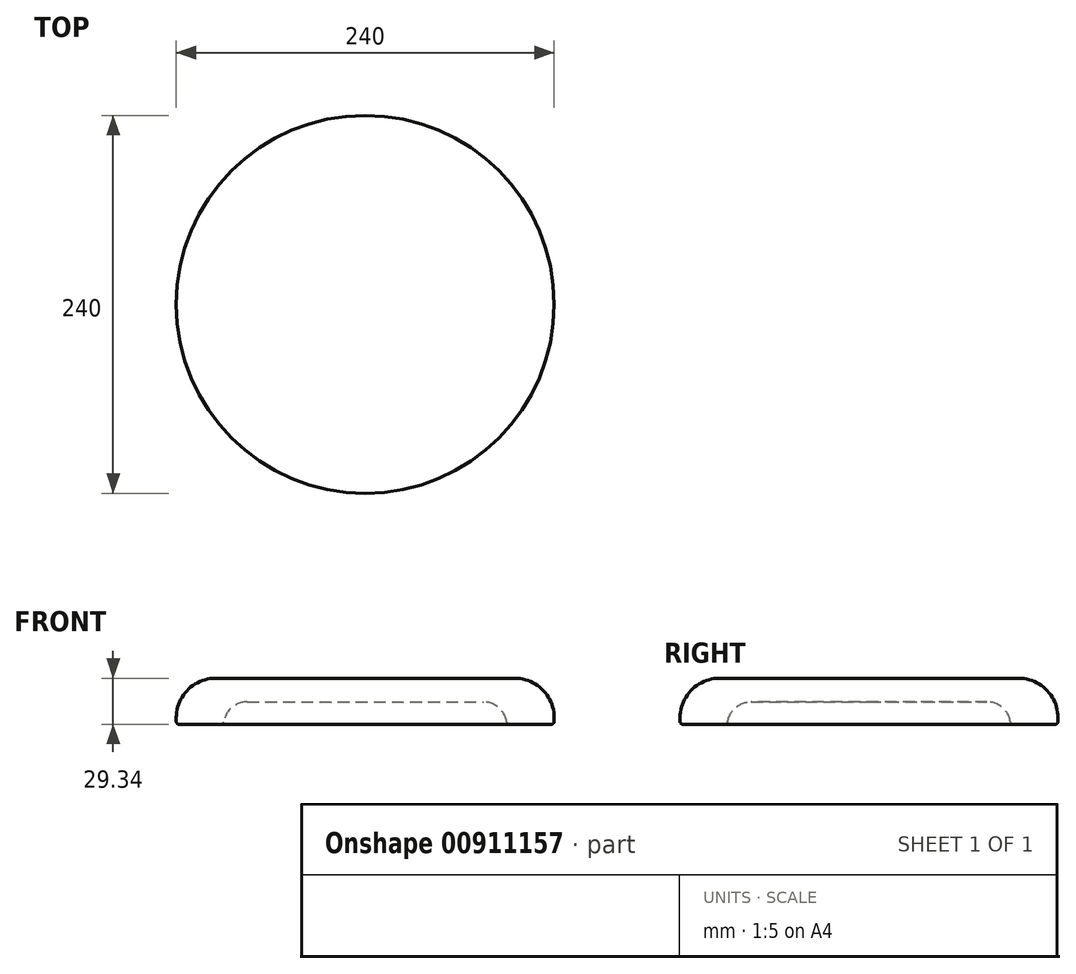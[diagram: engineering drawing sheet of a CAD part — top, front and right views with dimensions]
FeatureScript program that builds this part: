
annotation { "Feature Type Name" : "Feature", "Feature Type Description" : "" }
export const myFeature = defineFeature(function(context is Context, id is Id, definition is map)
    precondition{}
    {
        {
            var Q0;
            Q0=qCreatedBy(makeId("Front.planeOp"),FACE);
            var sketch = newSketch(context, id + "F0", { "sketchPlane" : qUnion([Q0])});
            skLineSegment(sketch, "E0", {"start": v(0, 0) * mm, "end": v(0, 15) * mm});
            skLineSegment(sketch, "E1", {"start": v(0, 15) * mm, "end": v(95, 15) * mm});
            skLineSegment(sketch, "E2", {"start": v(120, -10) * mm, "end": v(120, -12.34) * mm});
            skLineSegment(sketch, "E3", {"start": v(118, -14.34) * mm, "end": v(91.8, -14.34) * mm});
            skLineSegment(sketch, "E4", {"start": v(90, -15) * mm, "end": v(90, -14.34) * mm});
            skLineSegment(sketch, "E5", {"start": v(75, 0) * mm, "end": v(0, 0) * mm});
            skPoint(sketch, "E6.visualSharp", {"position": v(120, 15) * mm});
            skArc(sketch, "E6.filletArc", {"start": v(120, -10) * mm, "mid": v(112.68, 7.68) * mm, "end": v(95, 15) * mm});
            skPoint(sketch, "E7.visualSharp", {"position": v(90, 0) * mm});
            skArc(sketch, "E7.filletArc", {"start": v(89.82, -12.65) * mm, "mid": v(84.74, -3.6) * mm, "end": v(75, 0) * mm});
            skPoint(sketch, "E8.visualSharp", {"position": v(120, -14.34) * mm});
            skArc(sketch, "E8.filletArc", {"start": v(118, -14.34) * mm, "mid": v(119.41, -13.76) * mm, "end": v(120, -12.34) * mm});
            skArc(sketch, "E9.filletArc", {"start": v(89.82, -12.65) * mm, "mid": v(90.5, -13.86) * mm, "end": v(91.8, -14.34) * mm});
            skSolve(sketch);
        }
        {
            var Q0;
            Q0=makeQuery(id+"F0.imprint","IMPRINT",FACE,{"disambiguationData":[TD([[makeQuery(id+"F0.imprint","IMPRINT",EDGE,{"derivedFrom":sQuery(id+"F0.wireOp",EDGE,"E0")}),-1.0]])]});
            var Q1;
            Q1=sQuery(id+"F0.wireOp",EDGE,"E0");
            revolve(context, id + "F1", {"surfaceOperationType" : NewSurfaceOperationType.NEW, "entities" : qUnion([Q0]), "axis" : qUnion([Q1]), "revolveType" : RevolveType.FULL});
        }
    });
